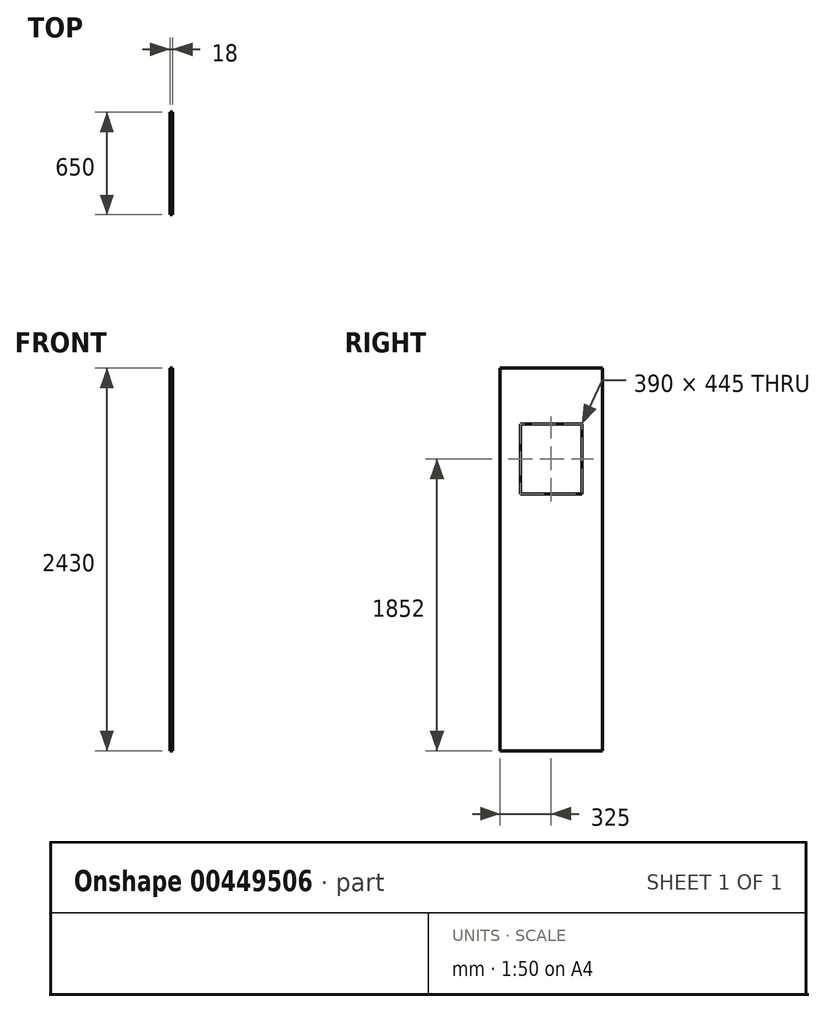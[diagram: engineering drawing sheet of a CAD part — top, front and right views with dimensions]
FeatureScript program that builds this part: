
annotation { "Feature Type Name" : "Feature", "Feature Type Description" : "" }
export const myFeature = defineFeature(function(context is Context, id is Id, definition is map)
    precondition{}
    {
        {
            var Q0;
            Q0=qCreatedBy(makeId("Right.planeOp"),FACE);
            var sketch = newSketch(context, id + "F0", { "sketchPlane" : qUnion([Q0])});
            skLineSegment(sketch, "E0.bottom", {"start": v(0, 2430) * mm, "end": v(650, 2430) * mm});
            skLineSegment(sketch, "E0.top", {"start": v(0, 0) * mm, "end": v(650, 0) * mm});
            skLineSegment(sketch, "E0.left", {"start": v(0, 2430) * mm, "end": v(0, 0) * mm});
            skLineSegment(sketch, "E0.right", {"start": v(650, 2430) * mm, "end": v(650, 0) * mm});
            skSolve(sketch);
        }
        {
            var Q0;
            Q0=qSketchRegion(id+"F0",true);
            extrude(context, id + "F1", {"entities" : qUnion([Q0]), "oppositeDirection" : true, "depth" : 18 * mm});
        }
        {
            var Q0;
            Q0=makeQuery(id+"F1.opExtrude","CAP_FACE",FACE,{"disambiguationData":[OSD([sQuery(id+"F0.wireOp",EDGE,"E0.bottom"),sQuery(id+"F0.wireOp",EDGE,"E0.top"),sQuery(id+"F0.wireOp",EDGE,"E0.left"),sQuery(id+"F0.wireOp",EDGE,"E0.right")])],"isStart":true});
            var sketch = newSketch(context, id + "F2", { "sketchPlane" : qUnion([Q0])});
            skLineSegment(sketch, "E1.bottom", {"start": v(130, 2074.5) * mm, "end": v(520, 2074.5) * mm});
            skLineSegment(sketch, "E1.top", {"start": v(130, 1629.5) * mm, "end": v(520, 1629.5) * mm});
            skLineSegment(sketch, "E1.left", {"start": v(130, 2074.5) * mm, "end": v(130, 1629.5) * mm});
            skLineSegment(sketch, "E1.right", {"start": v(520, 2074.5) * mm, "end": v(520, 1629.5) * mm});
            skSolve(sketch);
        }
        {
            var Q0;
            Q0 = qSketchRegion(id + "F2", true);
            extrude(context, id + "F3", {"entities" : qUnion([Q0]), "operationType" : NewBodyOperationType.REMOVE, "endBound" : BoundingType.THROUGH_ALL, "oppositeDirection" : true, "depth" : 25 * mm, "offsetDistance" : 25 * mm});
        }
    });
